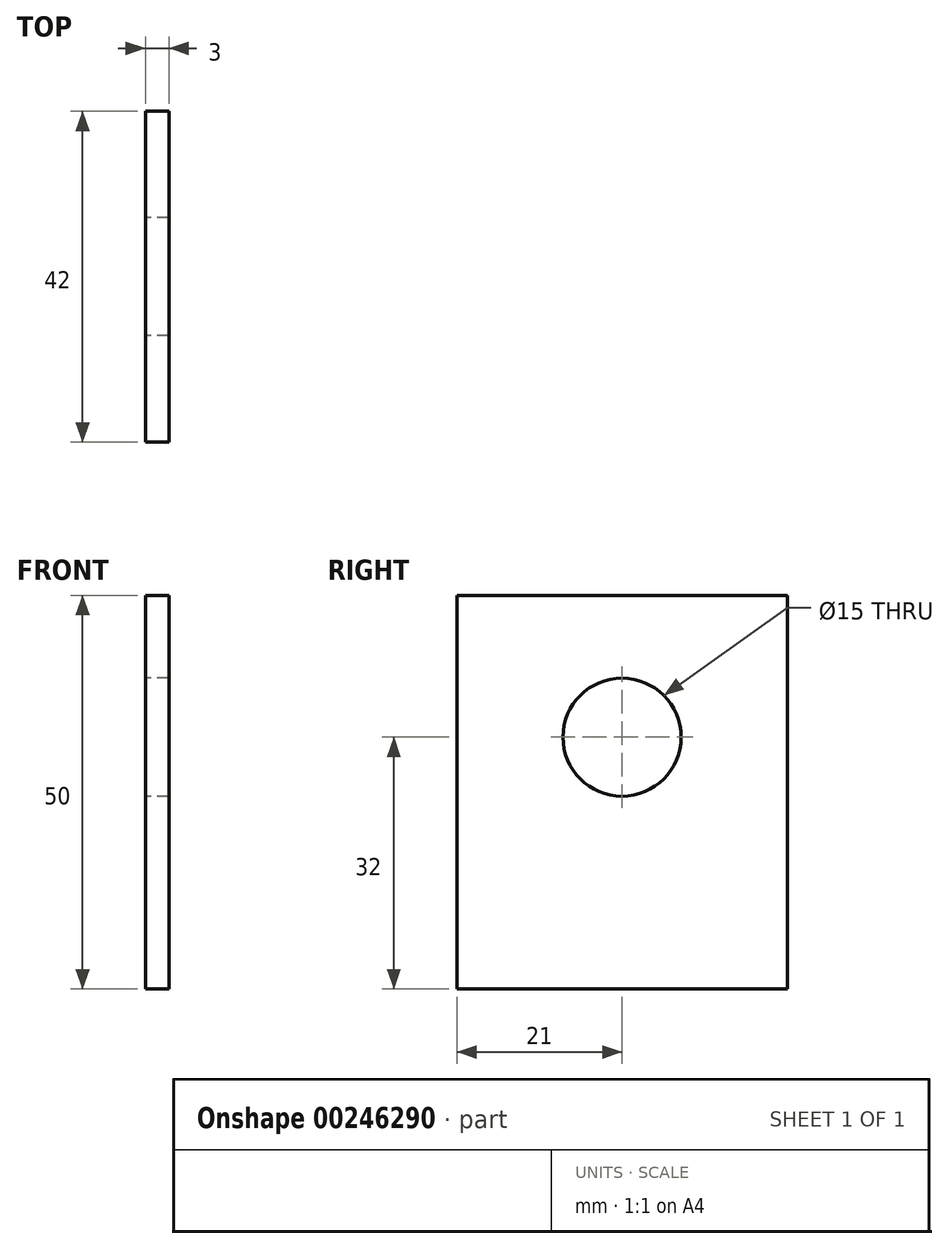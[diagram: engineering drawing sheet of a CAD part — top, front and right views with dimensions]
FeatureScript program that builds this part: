
annotation { "Feature Type Name" : "Feature", "Feature Type Description" : "" }
export const myFeature = defineFeature(function(context is Context, id is Id, definition is map)
    precondition{}
    {
        {
            var Q0;
            Q0=qCreatedBy(makeId("Right.planeOp"),FACE);
            var sketch = newSketch(context, id + "F0", { "sketchPlane" : qUnion([Q0])});
            skLineSegment(sketch, "E0.bottom", {"start": v(-21, 50) * mm, "end": v(21, 50) * mm});
            skLineSegment(sketch, "E0.top", {"start": v(-21, 0) * mm, "end": v(21, 0) * mm});
            skLineSegment(sketch, "E0.left", {"start": v(-21, 50) * mm, "end": v(-21, 0) * mm});
            skLineSegment(sketch, "E0.right", {"start": v(21, 50) * mm, "end": v(21, 0) * mm});
            skPoint(sketch, "E1", {"position": v(0, 50) * mm});
            skCircle(sketch, "E2", {"center": v(0, 32) * mm, "radius": 7.5 * mm});
            skSolve(sketch);
        }
        {
            var Q0;
            Q0 = qSketchRegion(id + "F0", true);
            extrude(context, id + "F1", {"entities" : qUnion([Q0]), "depth" : 3 * mm});
        }
    });
